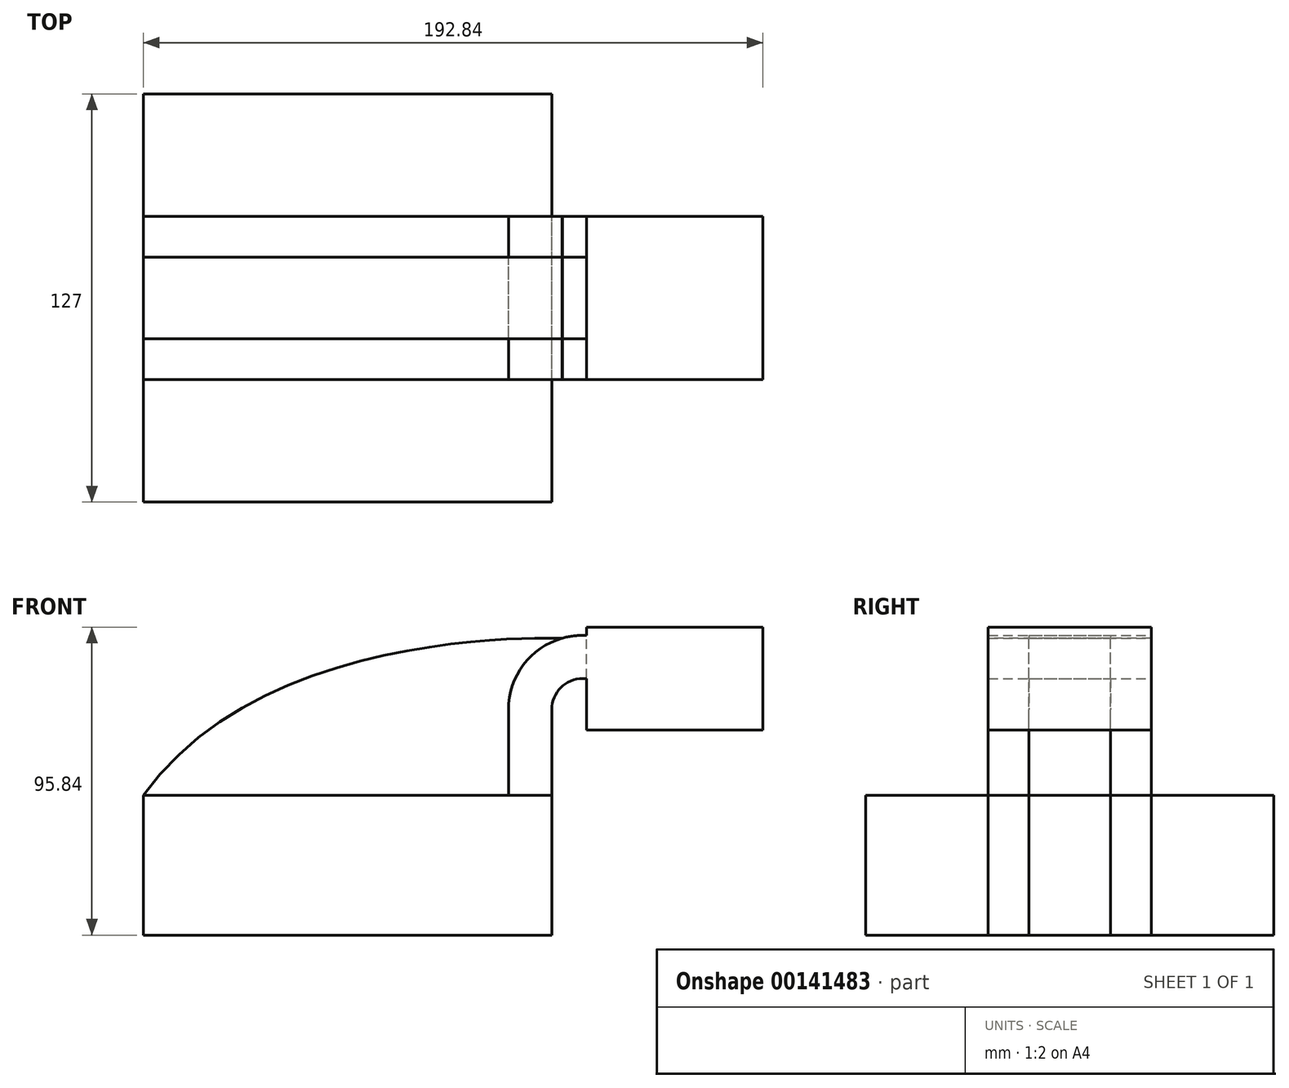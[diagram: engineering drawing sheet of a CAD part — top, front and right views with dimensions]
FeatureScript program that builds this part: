
annotation { "Feature Type Name" : "Feature", "Feature Type Description" : "" }
export const myFeature = defineFeature(function(context is Context, id is Id, definition is map)
    precondition{}
    {
        {
            var Q0;
            Q0=qCreatedBy(makeId("Front.planeOp"),FACE);
            var sketch = newSketch(context, id + "F0", { "sketchPlane" : qUnion([Q0])});
            skLineSegment(sketch, "E0.bottom", {"start": v(-63.53, -21.75) * mm, "end": v(63.53, -21.75) * mm});
            skLineSegment(sketch, "E0.top", {"start": v(-63.53, 21.75) * mm, "end": v(63.53, 21.75) * mm});
            skLineSegment(sketch, "E0.left", {"start": v(-63.53, -21.75) * mm, "end": v(-63.53, 21.75) * mm});
            skLineSegment(sketch, "E0.right", {"start": v(63.53, -21.75) * mm, "end": v(63.53, 21.75) * mm});
            skPoint(sketch, "E0.middle", {"position": v(0, 0) * mm});
            skLineSegment(sketch, "E1.bottom", {"start": v(74.33, 42.1) * mm, "end": v(129.3, 42.1) * mm});
            skLineSegment(sketch, "E1.top", {"start": v(74.33, 74.1) * mm, "end": v(129.3, 74.1) * mm});
            skLineSegment(sketch, "E1.left", {"start": v(74.33, 42.1) * mm, "end": v(74.33, 74.1) * mm});
            skLineSegment(sketch, "E1.right", {"start": v(129.3, 42.1) * mm, "end": v(129.3, 74.1) * mm});
            skPoint(sketch, "E1.middle", {"position": v(101.82, 58.1) * mm});
            skLineSegment(sketch, "E2", {"start": v(63.53, 21.75) * mm, "end": v(63.53, 48.46) * mm});
            skArc(sketch, "E3", {"start": v(63.53, 48.46) * mm, "mid": v(66.36, 55.28) * mm, "end": v(73.17, 58.1) * mm});
            skLineSegment(sketch, "E4", {"start": v(73.17, 58.1) * mm, "end": v(101.82, 58.1) * mm});
            skLineSegment(sketch, "E5.0", {"start": v(73.17, 71.56) * mm, "end": v(101.33, 71.56) * mm});
            skArc(sketch, "E5.1", {"start": v(50.07, 48.46) * mm, "mid": v(56.84, 64.8) * mm, "end": v(73.17, 71.56) * mm});
            skLineSegment(sketch, "E5.2", {"start": v(50.07, 21.75) * mm, "end": v(50.07, 48.46) * mm});
            skFitSpline(sketch, "E6", {"points": [v(-63.53, 21.75) * mm, v(66.79, 70.66) * mm, v(66.88, 70.69) * mm], "startDerivative": vector(116.9, 163.87) * mm, "endDerivative": vector(3.05, 1.47) * mm});
            skSolve(sketch);
        }
        {
            var Q0;
            {var subQ0=sQuery(id+"F0.wireOp",EDGE,"E6");var subQ1=sQuery(id+"F0.wireOp",EDGE,"E5.1");var subQ2=makeQuery(id+"F0.imprint","INTERSECT",VERTEX,{"disambiguationData":[OD(0.0)],"derivedFrom":[subQ1,subQ0]});Q0=makeQuery(id+"F0.imprint","IMPRINT",FACE,{"disambiguationData":[TD([[makeQuery(id+"F0.imprint","IMPRINT",EDGE,{"disambiguationData":[TD([[subQ2,1.0]])],"derivedFrom":subQ1}),-1.0]])]});}
            var Q1;
            Q1=makeQuery(id+"F0.imprint","IMPRINT",FACE,{"disambiguationData":[TD([[makeQuery(id+"F0.imprint","IMPRINT",EDGE,{"derivedFrom":sQuery(id+"F0.wireOp",EDGE,"E0.bottom")}),1.0]])]});
            extrude(context, id + "F1", {"entities" : qUnion([Q0, Q1]), "endBound" : BoundingType.SYMMETRIC, "depth" : 127 * mm});
        }
        {
            var Q0;
            {var subQ0=sQuery(id+"F0.wireOp",EDGE,"E6");var subQ1=sQuery(id+"F0.wireOp",EDGE,"E5.1");var subQ2=makeQuery(id+"F0.imprint","INTERSECT",VERTEX,{"disambiguationData":[OD(0.0)],"derivedFrom":[subQ1,subQ0]});Q0=makeQuery(id+"F0.imprint","IMPRINT",FACE,{"disambiguationData":[TD([[makeQuery(id+"F0.imprint","IMPRINT",EDGE,{"disambiguationData":[TD([[subQ2,1.0]])],"derivedFrom":subQ1}),-1.0]])]});}
            var Q1;
            Q1=makeQuery(id+"F0.imprint","IMPRINT",FACE,{"disambiguationData":[TD([[makeQuery(id+"F0.imprint","IMPRINT",EDGE,{"derivedFrom":sQuery(id+"F0.wireOp",EDGE,"E0.bottom")}),1.0]])]});
            var Q2;
            {var subQ1=sQuery(id+"F0.wireOp",EDGE,"E2");Q2=makeQuery(id+"F0.imprint","IMPRINT",FACE,{"disambiguationData":[TD([[makeQuery(id+"F0.imprint","IMPRINT",EDGE,{"derivedFrom":subQ1}),1.0]])]});}
            var Q3;
            {var subQ3=sQuery(id+"F0.wireOp",EDGE,"E1.bottom");Q3=makeQuery(id+"F0.imprint","IMPRINT",FACE,{"disambiguationData":[TD([[makeQuery(id+"F0.imprint","IMPRINT",EDGE,{"derivedFrom":subQ3}),1.0]])]});}
            extrude(context, id + "F2", {"entities" : qUnion([Q0, Q1, Q2, Q3]), "endBound" : BoundingType.SYMMETRIC, "depth" : 50.8 * mm});
        }
        {
            var Q0;
            {var subQ0=sQuery(id+"F0.wireOp",EDGE,"E6");var subQ1=sQuery(id+"F0.wireOp",EDGE,"E5.1");var subQ2=makeQuery(id+"F0.imprint","INTERSECT",VERTEX,{"disambiguationData":[OD(0.0)],"derivedFrom":[subQ1,subQ0]});Q0=makeQuery(id+"F0.imprint","IMPRINT",FACE,{"disambiguationData":[TD([[makeQuery(id+"F0.imprint","IMPRINT",EDGE,{"disambiguationData":[TD([[subQ2,1.0]])],"derivedFrom":subQ1}),-1.0]])]});}
            var Q1;
            Q1=makeQuery(id+"F0.imprint","IMPRINT",FACE,{"disambiguationData":[TD([[makeQuery(id+"F0.imprint","IMPRINT",EDGE,{"derivedFrom":sQuery(id+"F0.wireOp",EDGE,"E0.bottom")}),1.0]])]});
            var Q2;
            {var subQ1=sQuery(id+"F0.wireOp",EDGE,"E2");Q2=makeQuery(id+"F0.imprint","IMPRINT",FACE,{"disambiguationData":[TD([[makeQuery(id+"F0.imprint","IMPRINT",EDGE,{"derivedFrom":subQ1}),1.0]])]});}
            var Q3;
            {var subQ3=sQuery(id+"F0.wireOp",EDGE,"E5.2");Q3=makeQuery(id+"F0.imprint","IMPRINT",FACE,{"disambiguationData":[TD([[makeQuery(id+"F0.imprint","IMPRINT",EDGE,{"derivedFrom":subQ3}),1.0]])]});}
            extrude(context, id + "F3", {"entities" : qUnion([Q0, Q1, Q2, Q3]), "endBound" : BoundingType.SYMMETRIC, "depth" : 25.4 * mm});
        }
    });
